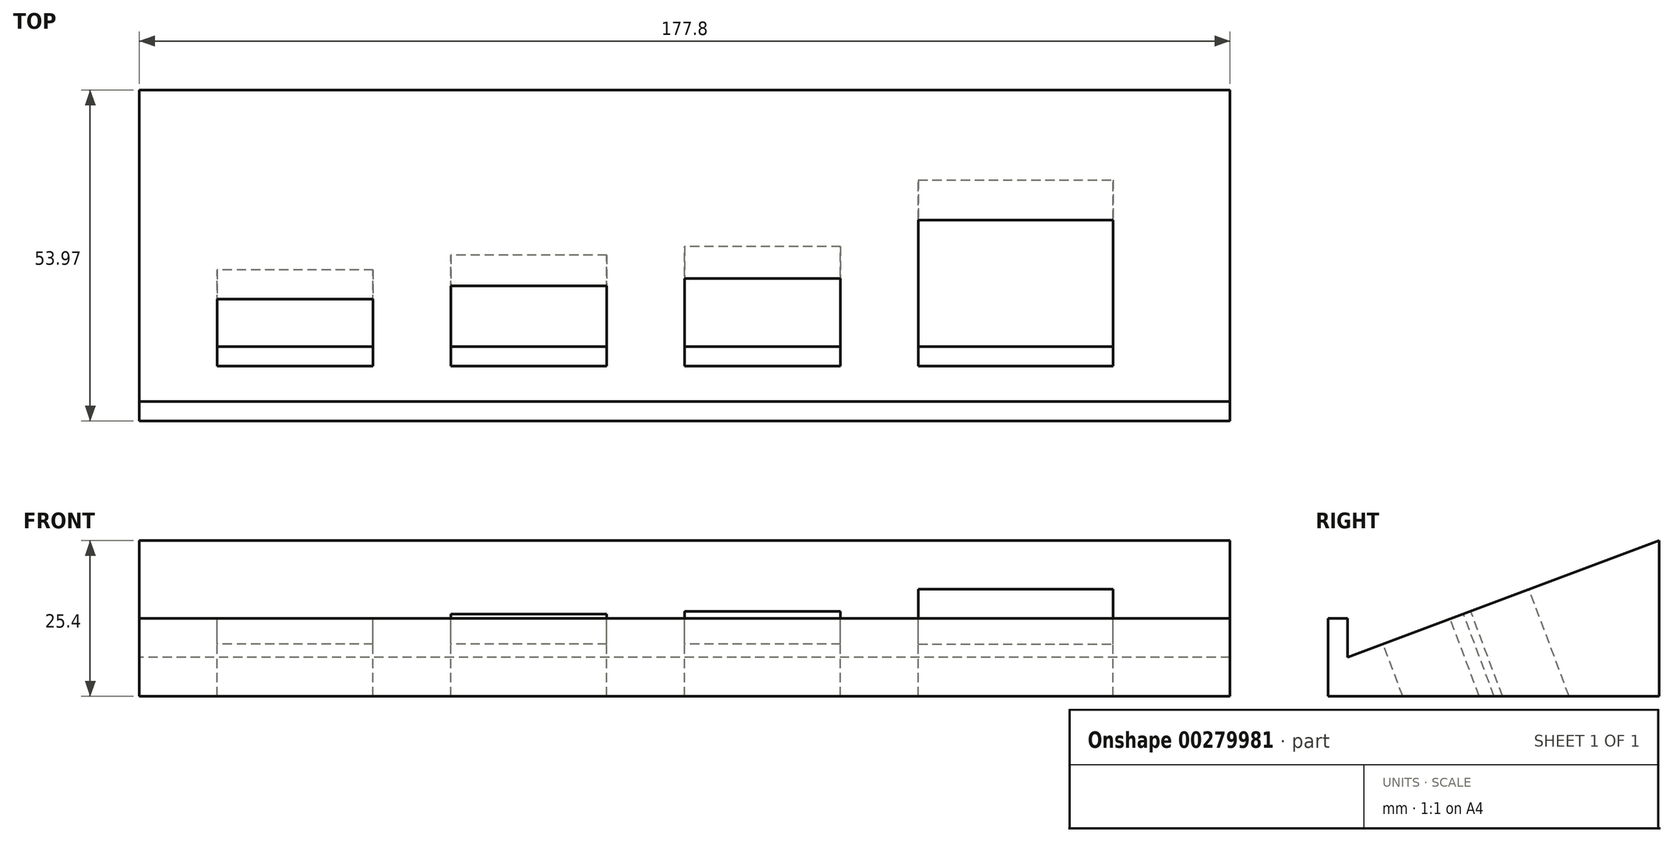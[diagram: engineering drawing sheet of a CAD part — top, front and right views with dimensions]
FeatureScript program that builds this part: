
annotation { "Feature Type Name" : "Feature", "Feature Type Description" : "" }
export const myFeature = defineFeature(function(context is Context, id is Id, definition is map)
    precondition{}
    {
        {
            var Q0;
            Q0=qCreatedBy(makeId("Right.planeOp"),FACE);
            var sketch = newSketch(context, id + "F0", { "sketchPlane" : qUnion([Q0])});
            skLineSegment(sketch, "E0.bottom", {"start": v(-39.9, 4.67) * mm, "end": v(10.9, 4.67) * mm});
            skLineSegment(sketch, "E0.top", {"start": v(-39.9, -1.68) * mm, "end": v(10.9, -1.68) * mm});
            skLineSegment(sketch, "E0.left", {"start": v(-39.9, 4.67) * mm, "end": v(-39.9, -1.68) * mm});
            skLineSegment(sketch, "E0.right", {"start": v(10.9, 4.67) * mm, "end": v(10.9, -1.68) * mm});
            skLineSegment(sketch, "E1", {"start": v(10.9, 4.67) * mm, "end": v(10.9, 23.72) * mm});
            skLineSegment(sketch, "E2", {"start": v(10.9, 23.72) * mm, "end": v(-39.9, 4.67) * mm});
            skLineSegment(sketch, "E3.bottom", {"start": v(-39.9, -1.68) * mm, "end": v(-43.08, -1.68) * mm});
            skLineSegment(sketch, "E3.top", {"start": v(-39.9, 11.02) * mm, "end": v(-43.08, 11.02) * mm});
            skLineSegment(sketch, "E3.left", {"start": v(-39.9, -1.68) * mm, "end": v(-39.9, 11.02) * mm});
            skLineSegment(sketch, "E3.right", {"start": v(-43.08, -1.68) * mm, "end": v(-43.08, 11.02) * mm});
            skSolve(sketch);
        }
        {
            var Q0;
            {var subQ0=sQuery(id+"F0.wireOp",EDGE,"E0.bottom");Q0=makeQuery(id+"F0.imprint","IMPRINT",FACE,{"disambiguationData":[TD([[makeQuery(id+"F0.imprint","IMPRINT",EDGE,{"derivedFrom":subQ0}),-1.0]])]});}
            var Q1;
            Q1=makeQuery(id+"F0.imprint","IMPRINT",FACE,{"disambiguationData":[TD([[makeQuery(id+"F0.imprint","IMPRINT",EDGE,{"derivedFrom":sQuery(id+"F0.wireOp",EDGE,"E0.bottom")}),1.0]])]});
            var Q2;
            {var subQ3=sQuery(id+"F0.wireOp",EDGE,"E3.bottom");Q2=makeQuery(id+"F0.imprint","IMPRINT",FACE,{"disambiguationData":[TD([[makeQuery(id+"F0.imprint","IMPRINT",EDGE,{"derivedFrom":subQ3}),-1.0]])]});}
            extrude(context, id + "F1", {"entities" : qUnion([Q0, Q1, Q2]), "depth" : 177.8 * mm});
        }
        {
            var Q0;
            Q0=makeQuery(id+"F1.opExtrude","SWEPT_FACE",FACE,{"disambiguationData":[OSD([sQuery(id+"F0.wireOp",EDGE,"E2")])]});
            var sketch = newSketch(context, id + "F2", { "sketchPlane" : qUnion([Q0])});
            skLineSegment(sketch, "E4.bottom", {"start": v(114.3, -29.55) * mm, "end": v(88.9, -29.55) * mm});
            skLineSegment(sketch, "E4.top", {"start": v(114.3, -14.31) * mm, "end": v(88.9, -14.31) * mm});
            skLineSegment(sketch, "E4.left", {"start": v(114.3, -29.55) * mm, "end": v(114.3, -14.31) * mm});
            skLineSegment(sketch, "E4.right", {"start": v(88.9, -29.55) * mm, "end": v(88.9, -14.31) * mm});
            skLineSegment(sketch, "E5.bottom", {"start": v(76.2, -29.55) * mm, "end": v(50.8, -29.55) * mm});
            skLineSegment(sketch, "E5.top", {"start": v(76.2, -15.58) * mm, "end": v(50.8, -15.58) * mm});
            skLineSegment(sketch, "E5.left", {"start": v(76.2, -29.55) * mm, "end": v(76.2, -15.58) * mm});
            skLineSegment(sketch, "E5.right", {"start": v(50.8, -29.55) * mm, "end": v(50.8, -15.58) * mm});
            skLineSegment(sketch, "E6.bottom", {"start": v(38.1, -29.55) * mm, "end": v(12.7, -29.55) * mm});
            skLineSegment(sketch, "E6.top", {"start": v(38.1, -17.87) * mm, "end": v(12.7, -17.87) * mm});
            skLineSegment(sketch, "E6.left", {"start": v(38.1, -29.55) * mm, "end": v(38.1, -17.87) * mm});
            skLineSegment(sketch, "E6.right", {"start": v(12.7, -29.55) * mm, "end": v(12.7, -17.87) * mm});
            skLineSegment(sketch, "E7", {"start": v(114.3, -29.55) * mm, "end": v(101.6, -29.55) * mm});
            skLineSegment(sketch, "E8", {"start": v(101.6, -29.55) * mm, "end": v(114.3, -29.55) * mm});
            skLineSegment(sketch, "E9.bottom", {"start": v(127, -29.55) * mm, "end": v(158.75, -29.55) * mm});
            skLineSegment(sketch, "E9.top", {"start": v(127, -4.15) * mm, "end": v(158.75, -4.15) * mm});
            skLineSegment(sketch, "E9.left", {"start": v(127, -29.55) * mm, "end": v(127, -4.15) * mm});
            skLineSegment(sketch, "E9.right", {"start": v(158.75, -29.55) * mm, "end": v(158.75, -4.15) * mm});
            skPoint(sketch, "E10.endSnap0", {"position": v(0, -8.6) * mm});
            skSolve(sketch);
        }
        {
            var Q0;
            Q0 = qSketchRegion(id + "F2", true);
            extrude(context, id + "F3", {"entities" : qUnion([Q0]), "operationType" : NewBodyOperationType.REMOVE, "oppositeDirection" : true, "depth" : 25.4 * mm});
        }
    });
